# Revit family: 712-7020-001-DN80-150
name_source: partatom
category: Pipe Accessories
units: mm (PartAtom-declared; Revit-internal decimal feet)

## family parameters
Always vertical = Yes
Cut with Voids When Loaded = No
Part Type = Breaks Into
Round Connector Dimension = Use Diameter
Shared = No
Work Plane-Based = No

## types (4) — shared parameters
DN080_PN10/16 = 712-0080-70-201
DN100 = No
DN100_PN10/16 = 712-0100-70-201
DN125 = No
DN125_PN10/16 = 712-0125-70-201
DN150 = No
DN150_PN10/16 = 712-0150-70-201
DN80 = No
Description_ = AVK DUCKFOOT BEND/LOOSE FLANGES
Hole = 5 mm  [stored 0.0164042 ft]
Search_Table = 712-7020-001-DN80-150
URL product pages = https://www.avkvalves.com

## per-type parameters (varying)
| type | Body_wallthickness | CH | D | D2 | F2 | FOD | Flange_thickness | H2 | H_width | ID | L | L_Ref | Nominal Diameter(DN) | RF_Thick | Rf_Dia | Rib_width | Rib_width_2 |
| DN080_PN10/16 | 95 mm | 53 mm | 180 mm  [stored 0.590551 ft] | 90 mm  [stored 0.295276 ft] | 34 mm | 100 mm  [stored 0.328084 ft] | 17 mm  [stored 0.0557743 ft] | 110 mm  [stored 0.360892 ft] | 7 mm  [stored 0.0229659 ft] | 40 mm  [stored 0.131234 ft] | 95 mm | 70 mm  [stored 0.229659 ft] | 80 mm  [stored 0.262467 ft] | 3 mm  [stored 0.00984252 ft] | 66 mm  [stored 0.216535 ft] | 20 mm  [stored 0.0656168 ft] | 10 mm  [stored 0.0328084 ft] |
| DN100_PN10/16 | 115 mm  [stored 0.377297 ft] | 63 mm | 200 mm  [stored 0.656168 ft] | 100 mm  [stored 0.328084 ft] | 34 mm | 110 mm  [stored 0.360892 ft] | 17 mm  [stored 0.0557743 ft] | 125 mm  [stored 0.410105 ft] | 7 mm  [stored 0.0229659 ft] | 50 mm  [stored 0.164042 ft] | 100 mm  [stored 0.328084 ft] | 80 mm  [stored 0.262467 ft] | 100 mm  [stored 0.328084 ft] | 3 mm  [stored 0.00984252 ft] | 78 mm  [stored 0.255906 ft] | 20 mm  [stored 0.0656168 ft] | 10 mm  [stored 0.0328084 ft] |
| DN125_PN10/16 | 140 mm  [stored 0.459318 ft] | 75 mm | 225 mm | 113 mm | 37 mm  [stored 0.121391 ft] | 125 mm  [stored 0.410105 ft] | 19 mm | 140 mm  [stored 0.459318 ft] | 7 mm  [stored 0.0229659 ft] | 63 mm | 110 mm  [stored 0.360892 ft] | 90 mm  [stored 0.295276 ft] | 125 mm  [stored 0.410105 ft] | 3 mm  [stored 0.00984252 ft] | 92 mm  [stored 0.301837 ft] | 20 mm  [stored 0.0656168 ft] | 10 mm  [stored 0.0328084 ft] |
| DN150_PN10/16 | 165 mm  [stored 0.541339 ft] | 88 mm | 250 mm | 125 mm  [stored 0.410105 ft] | 40 mm  [stored 0.131234 ft] | 143 mm | 20 mm  [stored 0.0656168 ft] | 160 mm  [stored 0.524934 ft] | 8 mm  [stored 0.0262467 ft] | 75 mm | 120 mm  [stored 0.393701 ft] | 100 mm  [stored 0.328084 ft] | 150 mm  [stored 0.492126 ft] | 4 mm  [stored 0.0131234 ft] | 106 mm | 25 mm  [stored 0.082021 ft] | 13 mm  [stored 0.0426509 ft] |

note: [stored X ft] marks values corroborated as IEEE doubles in the binary element streams (Revit-internal decimal feet)

## geometry (parser evidence)
native form markers: Sweep x5
no freeform markers — native parametric forms only
